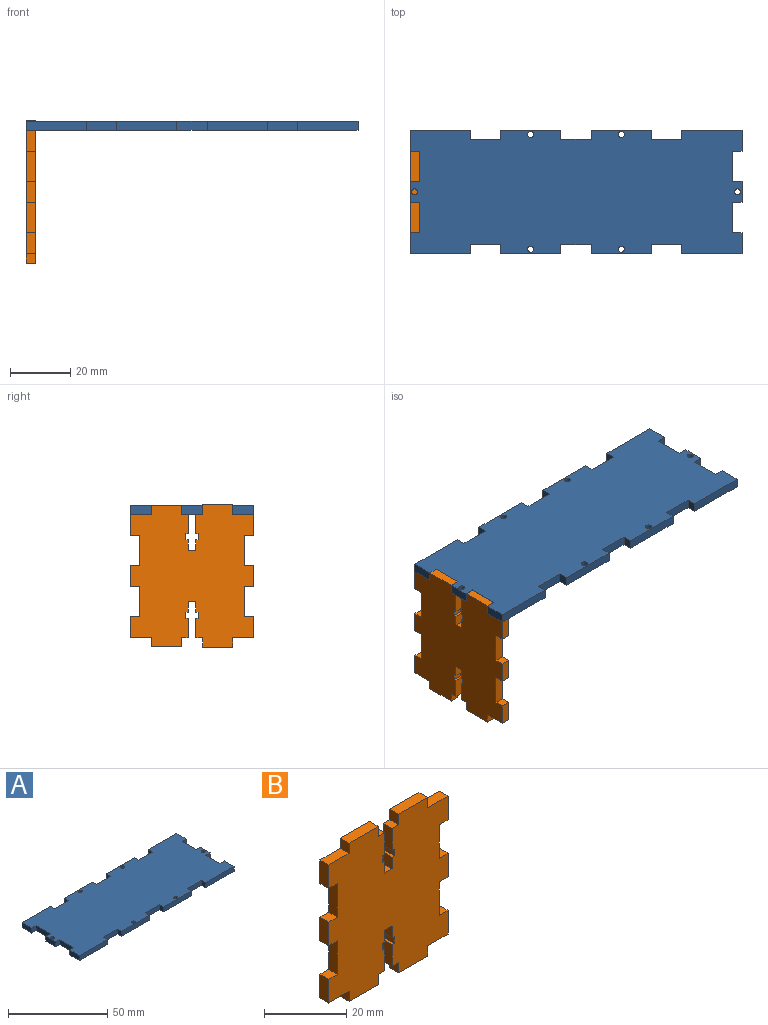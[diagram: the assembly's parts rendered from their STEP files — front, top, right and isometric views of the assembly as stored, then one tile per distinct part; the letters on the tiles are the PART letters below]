
ASSEMBLY  parts=2 mates=1
PART A: 52 faces, bbox 110x41x3 mm
  f0: plane 3x3mm, normal (-1,0,0), area 9mm2, adj f1,f46,f50,f51
  f1: plane 10x3mm, normal (0,1,0), area 30mm2, adj f0,f2,f50,f51
  f2: plane 3x3mm, normal (1,0,0), area 9mm2, adj f1,f3,f50,f51
  f3: plane 20x3mm, normal (0,1,0), area 60mm2, adj f2,f4,f50,f51
  f4: plane 3x3mm, normal (-1,0,0), area 9mm2, adj f3,f5,f50,f51
  f5: plane 10x3mm, normal (0,1,0), area 30mm2, adj f4,f6,f50,f51
  f6: plane 3x3mm, normal (1,0,0), area 9mm2, adj f5,f7,f50,f51
  f7: plane 20x3mm, normal (0,1,0), area 60mm2, adj f6,f8,f50,f51
  f8: plane 3x3mm, normal (-1,0,0), area 9mm2, adj f7,f9,f50,f51
  f9: plane 10x3mm, normal (0,1,0), area 30mm2, adj f8,f10,f50,f51
  f10: plane 3x3mm, normal (1,0,0), area 9mm2, adj f9,f11,f50,f51
  f11: plane 20x3mm, normal (0,1,0), area 60mm2, adj f10,f12,f50,f51
  f12: plane 7x3mm, normal (-1,0,0), area 21mm2, adj f11,f13,f50,f51
  f13: plane 3x3mm, normal (0,-1,0), area 9mm2, adj f12,f14,f50,f51
  f14: plane 10x3mm, normal (-1,0,0), area 30mm2, adj f13,f15,f50,f51
  f15: plane 3x3mm, normal (0,1,0), area 9mm2, adj f14,f16,f50,f51
  f16: plane 7x3mm, normal (-1,0,0), area 21mm2, adj f15,f17,f50,f51
  f17: plane 3x3mm, normal (0,-1,0), area 9mm2, adj f16,f18,f50,f51
  f18: plane 10x3mm, normal (-1,0,0), area 30mm2, adj f17,f19,f50,f51
  f19: plane 3x3mm, normal (0,1,0), area 9mm2, adj f18,f20,f50,f51
  f20: plane 7x3mm, normal (-1,0,0), area 21mm2, adj f19,f21,f50,f51
  f21: plane 20x3mm, normal (0,-1,0), area 60mm2, adj f20,f22,f50,f51
  f22: plane 3x3mm, normal (1,0,0), area 9mm2, adj f21,f23,f50,f51
  f23: plane 10x3mm, normal (0,-1,0), area 30mm2, adj f22,f24,f50,f51
  f24: plane 3x3mm, normal (-1,0,0), area 9mm2, adj f23,f25,f50,f51
  f25: plane 20x3mm, normal (0,-1,0), area 60mm2, adj f24,f26,f50,f51
  f26: plane 3x3mm, normal (1,0,0), area 9mm2, adj f25,f27,f50,f51
  f27: plane 10x3mm, normal (0,-1,0), area 30mm2, adj f26,f28,f50,f51
  f28: plane 3x3mm, normal (-1,0,0), area 9mm2, adj f27,f29,f50,f51
  f29: plane 20x3mm, normal (0,-1,0), area 60mm2, adj f28,f30,f50,f51
  f30: plane 3x3mm, normal (1,0,0), area 9mm2, adj f29,f31,f50,f51
  f31: plane 10x3mm, normal (0,-1,0), area 30mm2, adj f30,f32,f50,f51
  f32: plane 3x3mm, normal (-1,0,0), area 9mm2, adj f31,f33,f50,f51
  f33: plane 20x3mm, normal (0,-1,0), area 60mm2, adj f32,f34,f50,f51
  f34: plane 7x3mm, normal (1,0,0), area 21mm2, adj f33,f35,f50,f51
  f35: plane 3x3mm, normal (0,1,0), area 9mm2, adj f34,f36,f50,f51
  f36: plane 10x3mm, normal (1,0,0), area 30mm2, adj f35,f37,f50,f51
  f37: plane 3x3mm, normal (0,-1,0), area 9mm2, adj f36,f38,f50,f51
  f38: plane 7x3mm, normal (1,0,0), area 21mm2, adj f37,f39,f50,f51
  f39: plane 3x3mm, normal (0,1,0), area 9mm2, adj f38,f40,f50,f51
  f40: plane 10x3mm, normal (1,0,0), area 30mm2, adj f39,f41,f50,f51
  f41: plane 3x3mm, normal (0,-1,0), area 9mm2, adj f40,f42,f50,f51
  f42: plane 7x3mm, normal (1,0,0), area 21mm2, adj f41,f46,f50,f51
  f43: cylinder r=1mm len=3mm, axis (0,0,-1), area 18.8mm2, adj f50,f51
  f44: cylinder r=1mm len=3mm, axis (0,0,-1), area 18.8mm2, adj f50,f51
  f45: cylinder r=1mm len=3mm, axis (0,0,-1), area 18.8mm2, adj f50,f51
  f46: plane 20x3mm, normal (0,1,0), area 60mm2, adj f0,f42,f50,f51
  f47: cylinder r=1mm len=3mm, axis (0,0,-1), area 18.8mm2, adj f50,f51
  f48: cylinder r=1mm len=3mm, axis (0,0,-1), area 18.8mm2, adj f50,f51
  f49: cylinder r=1mm len=3mm, axis (0,0,-1), area 18.8mm2, adj f50,f51
  f50: plane 110x41mm, normal (0,0,1), area 4191.2mm2, adj f0,f1,f2,f3,f4,f5,f6,f7
  f51: plane 110x41mm, normal (0,0,-1), area 4191.2mm2, adj f0,f1,f2,f3,f4,f5,f6,f7
PART B: 62 faces, bbox 41x3x47.1 mm
  f0: plane 3.5x3mm, normal (-1,0,0), area 10.5mm2, adj f1,f59,f60,f61
  f1: plane 3x0.75mm, normal (0,0,-1), area 2.3mm2, adj f0,f2,f60,f61
  f2: plane 3x2mm, normal (-1,0,0), area 6mm2, adj f1,f3,f60,f61
  f3: plane 3x0.75mm, normal (0,0,1), area 2.3mm2, adj f2,f4,f60,f61
  f4: plane 6.5x3mm, normal (-1,0,0), area 19.5mm2, adj f3,f5,f60,f61
  f5: plane 3x2.25mm, normal (0,0,-1), area 6.8mm2, adj f4,f6,f60,f61
  f6: plane 3.07x3mm, normal (-1,0,0), area 9.2mm2, adj f5,f7,f60,f61
  f7: plane 10x3mm, normal (0,0,-1), area 30mm2, adj f6,f8,f60,f61
  f8: plane 3.07x3mm, normal (1,0,0), area 9.2mm2, adj f7,f9,f60,f61
  f9: plane 7x3mm, normal (0,0,-1), area 21mm2, adj f8,f10,f60,f61
  f10: plane 7x3mm, normal (1,0,0), area 21mm2, adj f9,f11,f60,f61
  f11: plane 3x3mm, normal (0,0,1), area 9mm2, adj f10,f12,f60,f61
  f12: plane 10x3mm, normal (1,0,0), area 30mm2, adj f11,f13,f60,f61
  f13: plane 3x3mm, normal (0,0,-1), area 9mm2, adj f12,f14,f60,f61
  f14: plane 7x3mm, normal (1,0,0), area 21mm2, adj f13,f15,f60,f61
  f15: plane 3x3mm, normal (0,0,1), area 9mm2, adj f14,f16,f60,f61
  f16: plane 10x3mm, normal (1,0,0), area 30mm2, adj f15,f17,f60,f61
  f17: plane 3x3mm, normal (0,0,-1), area 9mm2, adj f16,f18,f60,f61
  f18: plane 7x3mm, normal (1,0,0), area 21mm2, adj f17,f19,f60,f61
  f19: plane 7x3mm, normal (0,0,1), area 21mm2, adj f18,f20,f60,f61
  f20: plane 3.07x3mm, normal (1,0,0), area 9.2mm2, adj f19,f21,f60,f61
  f21: plane 10x3mm, normal (0,0,1), area 30mm2, adj f20,f22,f60,f61
  f22: plane 3.07x3mm, normal (-1,0,0), area 9.2mm2, adj f21,f23,f60,f61
  f23: plane 3x2.25mm, normal (0,0,1), area 6.8mm2, adj f22,f24,f60,f61
  f24: plane 6.5x3mm, normal (-1,0,0), area 19.5mm2, adj f23,f25,f60,f61
  f25: plane 3x0.75mm, normal (0,0,-1), area 2.3mm2, adj f24,f26,f60,f61
  f26: plane 3x2mm, normal (-1,0,0), area 6mm2, adj f25,f27,f60,f61
  f27: plane 3x0.75mm, normal (0,0,1), area 2.3mm2, adj f26,f28,f60,f61
  f28: plane 3.5x3mm, normal (-1,0,0), area 10.5mm2, adj f27,f29,f60,f61
  f29: plane 3x2.5mm, normal (0,0,1), area 7.5mm2, adj f28,f30,f60,f61
  f30: plane 3.5x3mm, normal (1,0,0), area 10.5mm2, adj f29,f31,f60,f61
  f31: plane 3x0.75mm, normal (0,0,1), area 2.3mm2, adj f30,f32,f60,f61
  f32: plane 3x2mm, normal (1,0,0), area 6mm2, adj f31,f33,f60,f61
  f33: plane 3x0.75mm, normal (0,0,-1), area 2.3mm2, adj f32,f34,f60,f61
  f34: plane 6.5x3mm, normal (1,0,0), area 19.5mm2, adj f33,f35,f60,f61
  f35: plane 3x2.25mm, normal (0,0,1), area 6.7mm2, adj f34,f36,f60,f61
  f36: plane 3x3mm, normal (1,0,0), area 9mm2, adj f35,f37,f60,f61
  f37: plane 10x3mm, normal (0,0,1), area 30mm2, adj f36,f38,f60,f61
  f38: plane 3x3mm, normal (-1,0,0), area 9mm2, adj f37,f39,f60,f61
  f39: plane 7x3mm, normal (0,0,1), area 21mm2, adj f38,f40,f60,f61
  f40: plane 7x3mm, normal (-1,0,0), area 21mm2, adj f39,f41,f60,f61
  f41: plane 3x3mm, normal (0,0,-1), area 9mm2, adj f40,f42,f60,f61
  f42: plane 10x3mm, normal (-1,0,0), area 30mm2, adj f41,f43,f60,f61
  f43: plane 3x3mm, normal (0,0,1), area 9mm2, adj f42,f44,f60,f61
  f44: plane 7x3mm, normal (-1,0,0), area 21mm2, adj f43,f45,f60,f61
  f45: plane 3x3mm, normal (0,0,-1), area 9mm2, adj f44,f46,f60,f61
  f46: plane 10x3mm, normal (-1,0,0), area 30mm2, adj f45,f47,f60,f61
  f47: plane 3x3mm, normal (0,0,1), area 9mm2, adj f46,f48,f60,f61
  f48: plane 7x3mm, normal (-1,0,0), area 21mm2, adj f47,f49,f60,f61
  f49: plane 7x3mm, normal (0,0,-1), area 21mm2, adj f48,f50,f60,f61
  f50: plane 3x3mm, normal (-1,0,0), area 9mm2, adj f49,f51,f60,f61
  f51: plane 10x3mm, normal (0,0,-1), area 30mm2, adj f50,f52,f60,f61
  f52: plane 3x3mm, normal (1,0,0), area 9mm2, adj f51,f53,f60,f61
  f53: plane 3x2.25mm, normal (0,0,-1), area 6.7mm2, adj f52,f54,f60,f61
  f54: plane 6.5x3mm, normal (1,0,0), area 19.5mm2, adj f53,f55,f60,f61
  f55: plane 3x0.75mm, normal (0,0,1), area 2.3mm2, adj f54,f56,f60,f61
  f56: plane 3x2mm, normal (1,0,0), area 6mm2, adj f55,f57,f60,f61
  f57: plane 3x0.75mm, normal (0,0,-1), area 2.3mm2, adj f56,f58,f60,f61
  f58: plane 3.5x3mm, normal (1,0,0), area 10.5mm2, adj f57,f59,f60,f61
  f59: plane 3x2.5mm, normal (0,0,-1), area 7.5mm2, adj f0,f58,f60,f61
  f60: plane 47.15x41mm, normal (0,-1,0), area 1616.5mm2, adj f0,f1,f2,f3,f4,f5,f6,f7
  f61: plane 47.15x41mm, normal (0,1,0), area 1616.5mm2, adj f0,f1,f2,f3,f4,f5,f6,f7
PLACE A t=(-26.59,-5.2,-1.65)mm
PLACE B rot(axis=(0,0,-1),90deg) t=(-25.09,35.8,-3.15)mm
MATE fastened B.f36 <-> A.f15  axis (0,-1,0) through (-25.09,18.8,-1.65)mm
